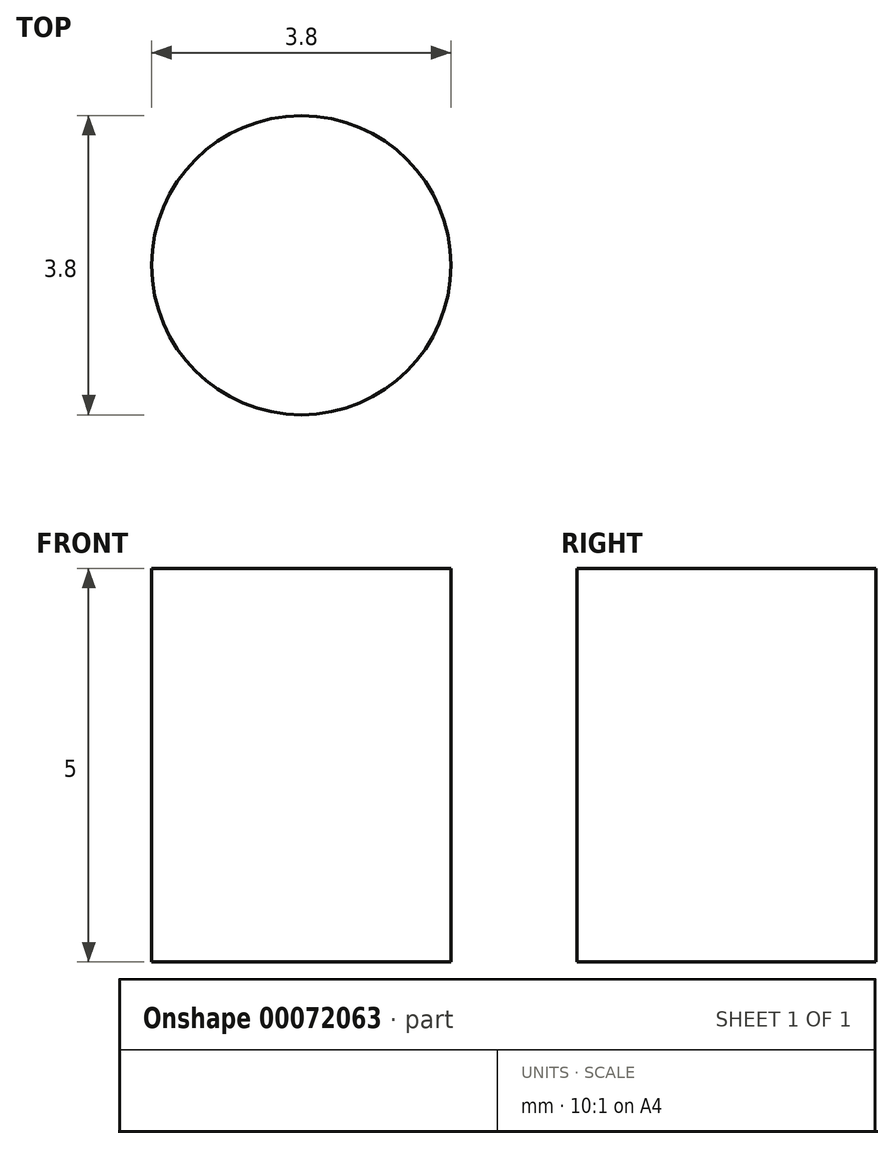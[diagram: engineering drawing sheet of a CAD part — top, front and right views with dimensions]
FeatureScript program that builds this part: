
annotation { "Feature Type Name" : "Feature", "Feature Type Description" : "" }
export const myFeature = defineFeature(function(context is Context, id is Id, definition is map)
    precondition{}
    {
        {
            var Q0;
            Q0=qCreatedBy(makeId("Top.planeOp"),FACE);
            var sketch = newSketch(context, id + "F0", { "sketchPlane" : qUnion([Q0])});
            skCircle(sketch, "E0", {"center": v(0, 0) * mm, "radius": 1.9 * mm});
            skSolve(sketch);
        }
        {
            var Q0;
            Q0=qSketchRegion(id+"F0",true);
            extrude(context, id + "F1", {"entities" : qUnion([Q0]), "depth" : 5 * mm});
        }
    });
